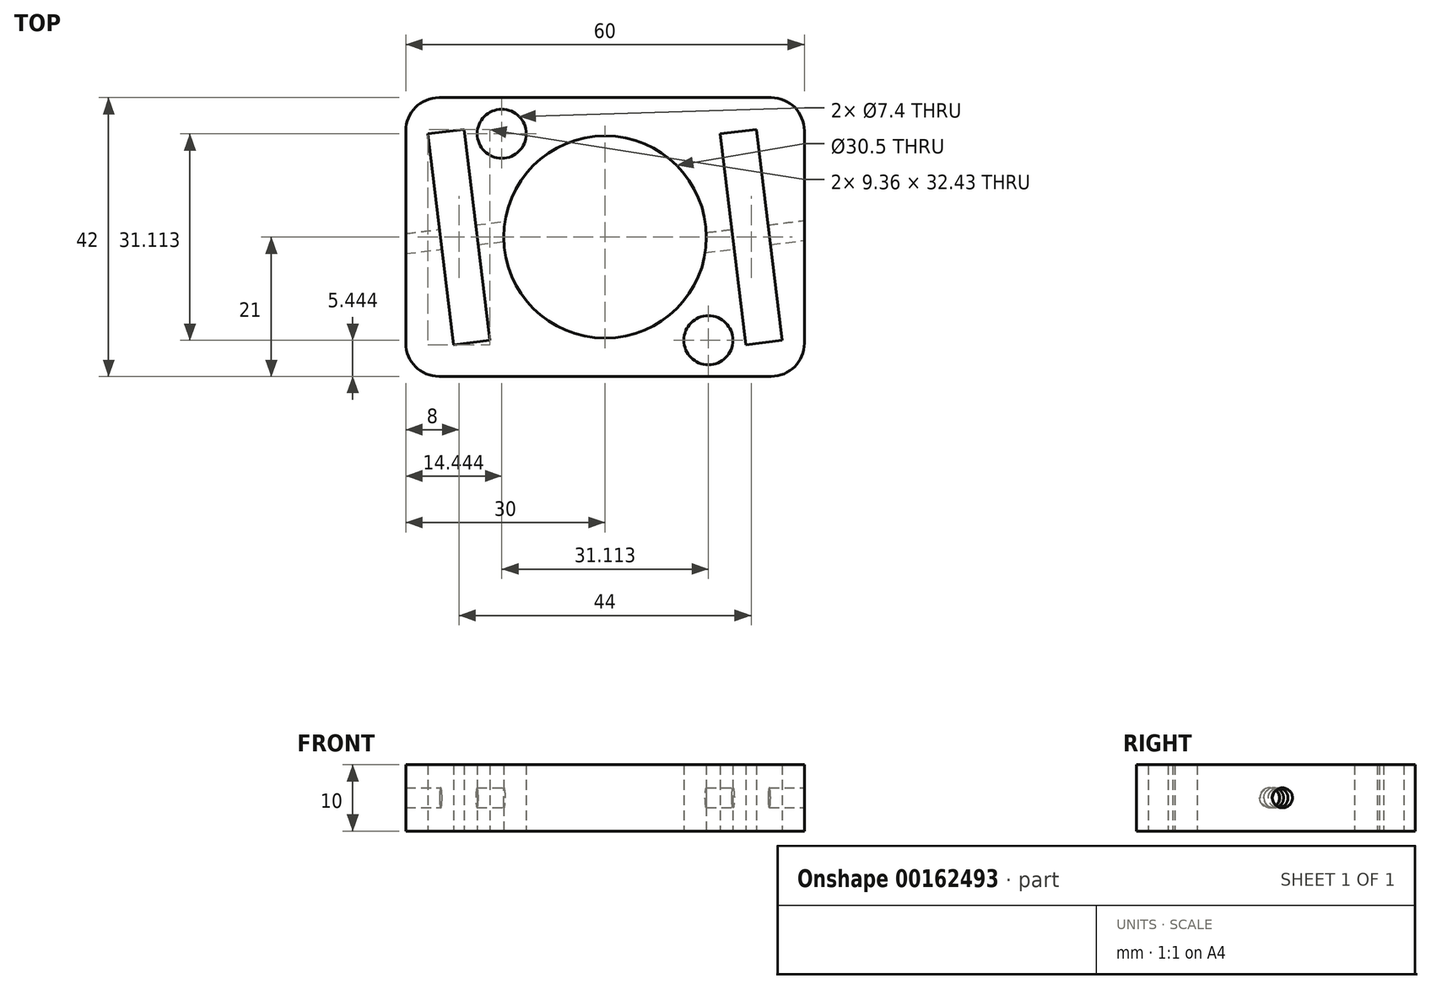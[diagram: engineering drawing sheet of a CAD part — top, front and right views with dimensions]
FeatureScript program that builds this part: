
annotation { "Feature Type Name" : "Feature", "Feature Type Description" : "" }
export const myFeature = defineFeature(function(context is Context, id is Id, definition is map)
    precondition{}
    {
        {
            var Q0;
            Q0=qCreatedBy(makeId("Top.planeOp"),FACE);
            var sketch = newSketch(context, id + "F0", { "sketchPlane" : qUnion([Q0])});
            skCircle(sketch, "E0", {"center": v(0, 0) * mm, "radius": 15.25 * mm});
            skLineSegment(sketch, "E1", {"start": v(22, 0) * mm, "end": v(43.67, 2.66) * mm, "construction": true});
            skLineSegment(sketch, "E2", {"start": v(24.73, 0.34) * mm, "end": v(22.78, 16.22) * mm});
            skLineSegment(sketch, "E3", {"start": v(22.78, 16.22) * mm, "end": v(17.32, 15.55) * mm});
            skLineSegment(sketch, "E4.MirrorCS", {"start": v(24.73, 0.34) * mm, "end": v(26.68, -15.55) * mm});
            skLineSegment(sketch, "E5.MirrorCS", {"start": v(26.68, -15.55) * mm, "end": v(21.22, -16.22) * mm});
            skLineSegment(sketch, "E6", {"start": v(0, 0) * mm, "end": v(0, 32.24) * mm, "construction": true});
            skLineSegment(sketch, "E7", {"start": v(-22, 0) * mm, "end": v(-3.75, 2.24) * mm, "construction": true});
            skLineSegment(sketch, "E8", {"start": v(-19.27, 0.34) * mm, "end": v(-21.22, 16.22) * mm});
            skLineSegment(sketch, "E9", {"start": v(-21.22, 16.22) * mm, "end": v(-26.68, 15.55) * mm});
            skLineSegment(sketch, "E10.MirrorCS", {"start": v(-19.27, 0.34) * mm, "end": v(-17.32, -15.55) * mm});
            skLineSegment(sketch, "E11.MirrorCS", {"start": v(-17.32, -15.55) * mm, "end": v(-22.78, -16.22) * mm});
            skLineSegment(sketch, "E12", {"start": v(-26.68, 15.55) * mm, "end": v(-24.73, -0.34) * mm});
            skLineSegment(sketch, "E13.MirrorCS", {"start": v(-22.78, -16.22) * mm, "end": v(-24.73, -0.34) * mm});
            skLineSegment(sketch, "E14", {"start": v(0, 0) * mm, "end": v(13.08, -13.08) * mm, "construction": true});
            skCircle(sketch, "E15", {"center": v(15.56, -15.56) * mm, "radius": 3.7 * mm});
            skLineSegment(sketch, "E16", {"start": v(0, 0) * mm, "end": v(8.08, 8.08) * mm, "construction": true});
            skCircle(sketch, "E17.MirrorC", {"center": v(-15.56, 15.56) * mm, "radius": 3.7 * mm});
            skLineSegment(sketch, "E18", {"start": v(0, 21) * mm, "end": v(25, 21) * mm});
            skLineSegment(sketch, "E19", {"start": v(30, 16) * mm, "end": v(30, 0) * mm});
            skLineSegment(sketch, "E20", {"start": v(0, 0) * mm, "end": v(13.67, 0) * mm, "construction": true});
            skLineSegment(sketch, "E21.MirrorCS", {"start": v(0, -21) * mm, "end": v(25, -21) * mm});
            skLineSegment(sketch, "E22.MirrorCS", {"start": v(30, -16) * mm, "end": v(30, 0) * mm});
            skLineSegment(sketch, "E23.MirrorCS", {"start": v(0, 21) * mm, "end": v(-25, 21) * mm});
            skLineSegment(sketch, "E24.MirrorCS", {"start": v(-30, 16) * mm, "end": v(-30, 0) * mm});
            skLineSegment(sketch, "E25.MirrorCS", {"start": v(-30, -16) * mm, "end": v(-30, 0) * mm});
            skLineSegment(sketch, "E26.MirrorCS", {"start": v(0, -21) * mm, "end": v(-25, -21) * mm});
            skPoint(sketch, "E27.visualSharp", {"position": v(30, 21) * mm});
            skArc(sketch, "E27.filletArc", {"start": v(30, 16) * mm, "mid": v(28.54, 19.54) * mm, "end": v(25, 21) * mm});
            skPoint(sketch, "E28.visualSharp", {"position": v(30, -21) * mm});
            skArc(sketch, "E28.filletArc", {"start": v(25, -21) * mm, "mid": v(28.54, -19.54) * mm, "end": v(30, -16) * mm});
            skPoint(sketch, "E29.visualSharp", {"position": v(-30, -21) * mm});
            skArc(sketch, "E29.filletArc", {"start": v(-30, -16) * mm, "mid": v(-28.54, -19.54) * mm, "end": v(-25, -21) * mm});
            skPoint(sketch, "E30.visualSharp", {"position": v(-30, 21) * mm});
            skArc(sketch, "E30.filletArc", {"start": v(-25, 21) * mm, "mid": v(-28.54, 19.54) * mm, "end": v(-30, 16) * mm});
            skLineSegment(sketch, "E31", {"start": v(17.32, 15.55) * mm, "end": v(21.22, -16.22) * mm});
            skSolve(sketch);
        }
        {
            var Q0;
            Q0 = qSketchRegion(id + "F0", true);
            extrude(context, id + "F1", {"entities" : qUnion([Q0]), "depth" : 10 * mm});
        }
        {
            var Q0;
            Q0=makeQuery(id+"F1.opExtrude","SWEPT_FACE",FACE,{"disambiguationData":[OSD([sQuery(id+"F0.wireOp",EDGE,"E8"),sQuery(id+"F0.wireOp",EDGE,"E10.MirrorCS")])]});
            var sketch = newSketch(context, id + "F2", { "sketchPlane" : qUnion([Q0])});
            skLineSegment(sketch, "E32", {"start": v(-2.68, 0) * mm, "end": v(-2.68, 10) * mm, "construction": true});
            skCircle(sketch, "E33", {"center": v(-2.68, 5) * mm, "radius": 1.5 * mm});
            skSolve(sketch);
        }
        {
            var Q0;
            Q0 = qSketchRegion(id + "F2", true);
            extrude(context, id + "F3", {"entities" : qUnion([Q0]), "operationType" : NewBodyOperationType.REMOVE, "endBound" : BoundingType.SYMMETRIC, "depth" : 25 * mm});
        }
        {
            var Q0;
            Q0=makeQuery(id+"F1.opExtrude","SWEPT_FACE",FACE,{"disambiguationData":[OSD([sQuery(id+"F0.wireOp",EDGE,"E31")])]});
            var sketch = newSketch(context, id + "F4", { "sketchPlane" : qUnion([Q0])});
            skLineSegment(sketch, "E34", {"start": v(-2.68, 10) * mm, "end": v(-2.68, 0) * mm, "construction": true});
            skCircle(sketch, "E35", {"center": v(-2.68, 5) * mm, "radius": 1.5 * mm});
            skSolve(sketch);
        }
        {
            var Q0;
            Q0 = qSketchRegion(id + "F4", true);
            extrude(context, id + "F5", {"entities" : qUnion([Q0]), "operationType" : NewBodyOperationType.REMOVE, "endBound" : BoundingType.SYMMETRIC, "oppositeDirection" : true, "depth" : 25 * mm});
        }
    });
